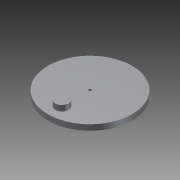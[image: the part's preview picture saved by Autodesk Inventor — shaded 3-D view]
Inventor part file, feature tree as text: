
AUTODESK INVENTOR PART (.ipt)
format: ipt  version: 2011 (Build 150239000, 239)  size: 79,872 bytes
history: native  units: mm
features: extrude x2, sketch x2, other x1
ambient origin geometry x8: Origin, YZ Plane, XZ Plane, XY Plane, X Axis, Y Axis, Z Axis, Center Point
feature tree (5):
  other  "Sólido1"
  extrude  "Extrusión1"  Depth=1.0mm
  extrude  "Extrusión2"  Depth=4.7mm
  sketch  "Boceto1"  dims[d0=30.0mm d1=1.0mm]
  sketch  "Boceto2"  dims[d2=2.0mm d3=0.0mm d4=4.7mm d6=10.0mm d7=2.0mm d8=0.0mm]
